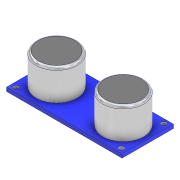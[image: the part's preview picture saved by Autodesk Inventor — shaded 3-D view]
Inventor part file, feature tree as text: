
AUTODESK INVENTOR PART (.ipt)
format: ipt  version: 2020 (Build 240168000, 168)  size: 167,424 bytes
history: mixed  units: mm
features: fillet x1, imported_body x1
ambient origin geometry x8: Origin, YZ Plane, XZ Plane, XY Plane, X Axis, Y Axis, Z Axis, Center Point
bodies: Solid1 (imported_parasolid)
feature tree (2):
  fillet  "Fillet1"  [1 undecoded]
  imported_body  NMx_Import_Brep_tag  [imported B-rep: ~16 faces, bbox_mm=[45.0, 13.5, 20.0]]
note: 1 required parameter value undecoded (feature->parameter linkage not recoverable at this tier; creation-order binding heuristic only, values carry confidence <= 0.55)
